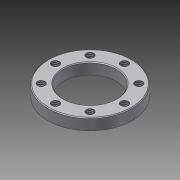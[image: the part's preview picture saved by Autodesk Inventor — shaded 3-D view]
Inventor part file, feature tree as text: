
AUTODESK INVENTOR PART (.ipt)
format: ipt  version: 2014 SP1 (Build 180222100, 222)  size: 120,832 bytes
history: native  units: in
note: dims shown in document units (in); Inventor stores cm internally (conversion verified against a paired STEP export)
features: thread x8, extrude x1, chamfer x1, sketch x1
ambient origin geometry x8: Origin, YZ Plane, XZ Plane, XY Plane, X Axis, Y Axis, Z Axis, Center Point
bodies: Solid1 (feature_tree)
feature tree (11):
  extrude  "Extrusion1"  Depth=0.125in
  thread  "Thread1"  [1 undecoded]
  thread  "Thread2"  [1 undecoded]
  thread  "Thread3"  [1 undecoded]
  thread  "Thread4"  [1 undecoded]
  thread  "Thread5"  [1 undecoded]
  thread  "Thread6"  [1 undecoded]
  thread  "Thread7"  [1 undecoded]
  thread  "Thread8"  [1 undecoded]
  chamfer  "Chamfer1"  Distance=1.0in
  sketch  "Sketch1"  dims[d0=2.8in d1=1.75in d2=1.15in d3=0.25in d4=3.1496in d6=360.0deg d8=0.375in d9=0.0in d10=1.0in d11=0.0in d12=1.0in d13=0.0in d14=1.0in d15=0.0in d16=1.0in d17=0.0in d18=1.0in d19=0.0in d20=1.0in d21=0.0in d22=1.0in d23=0.0in d24=1.0in d25=0.0in d26=0.025in d27=0.125in d28=45.0deg]
note: 8 required parameter values undecoded (feature->parameter linkage not recoverable at this tier; creation-order binding heuristic only, values carry confidence <= 0.55)
